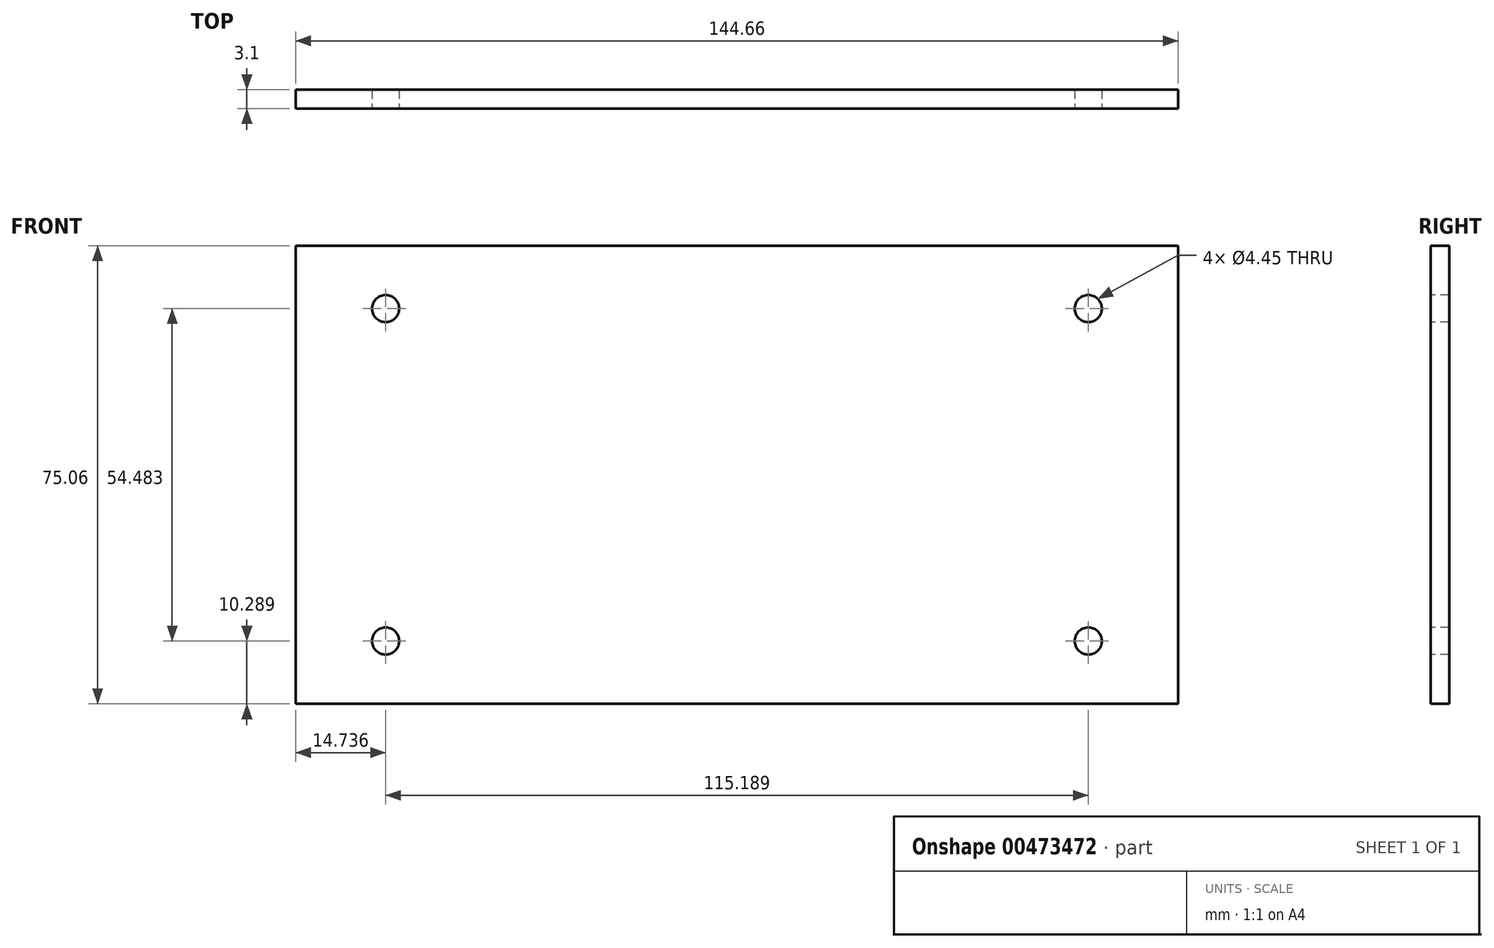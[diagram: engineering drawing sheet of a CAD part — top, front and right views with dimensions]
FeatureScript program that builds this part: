
annotation { "Feature Type Name" : "Feature", "Feature Type Description" : "" }
export const myFeature = defineFeature(function(context is Context, id is Id, definition is map)
    precondition{}
    {
        {
            var Q0;
            Q0=qCreatedBy(makeId("Front.planeOp"),FACE);
            var sketch = newSketch(context, id + "F0", { "sketchPlane" : qUnion([Q0])});
            skLineSegment(sketch, "E0.bottom", {"start": v(-72.33, 37.53) * mm, "end": v(72.33, 37.53) * mm});
            skLineSegment(sketch, "E0.top", {"start": v(-72.33, -37.53) * mm, "end": v(72.33, -37.53) * mm});
            skLineSegment(sketch, "E0.left", {"start": v(-72.33, 37.53) * mm, "end": v(-72.33, -37.53) * mm});
            skLineSegment(sketch, "E0.right", {"start": v(72.33, 37.53) * mm, "end": v(72.33, -37.53) * mm});
            skLineSegment(sketch, "E1", {"start": v(0, 0) * mm, "end": v(0, 37.53) * mm, "construction": true});
            skLineSegment(sketch, "E2", {"start": v(0, 0) * mm, "end": v(0, -37.53) * mm, "construction": true});
            skLineSegment(sketch, "E3", {"start": v(-72.33, 0) * mm, "end": v(0, 0) * mm, "construction": true});
            skLineSegment(sketch, "E4", {"start": v(0, 0) * mm, "end": v(72.33, 0) * mm, "construction": true});
            skSolve(sketch);
        }
        {
            var Q0;
            Q0=makeQuery(id+"F0.imprint","IMPRINT",FACE,{"disambiguationData":[TD([[makeQuery(id+"F0.imprint","IMPRINT",EDGE,{"derivedFrom":sQuery(id+"F0.wireOp",EDGE,"E0.bottom")}),-1.0]])]});
            extrude(context, id + "F1", {"entities" : qUnion([Q0]), "oppositeDirection" : true, "depth" : 3.1 * mm});
        }
        {
            var Q0;
            Q0=makeQuery(id+"F1.opExtrude","CAP_FACE",FACE,{"disambiguationData":[OSD([sQuery(id+"F0.wireOp",EDGE,"E0.bottom"),sQuery(id+"F0.wireOp",EDGE,"E0.top"),sQuery(id+"F0.wireOp",EDGE,"E0.left"),sQuery(id+"F0.wireOp",EDGE,"E0.right")])],"isStart":true});
            var sketch = newSketch(context, id + "F2", { "sketchPlane" : qUnion([Q0])});
            skCircle(sketch, "E5", {"center": v(-57.6, 27.24) * mm, "radius": 2.22 * mm});
            skCircle(sketch, "E6", {"center": v(-57.6, -27.24) * mm, "radius": 2.22 * mm});
            skCircle(sketch, "E7", {"center": v(57.6, -27.24) * mm, "radius": 2.22 * mm});
            skCircle(sketch, "E8", {"center": v(57.6, 27.24) * mm, "radius": 2.22 * mm});
            skSolve(sketch);
        }
        {
            var Q0;
            Q0 = qSketchRegion(id + "F2", true);
            extrude(context, id + "F3", {"entities" : qUnion([Q0]), "operationType" : NewBodyOperationType.REMOVE, "endBound" : BoundingType.UP_TO_NEXT, "oppositeDirection" : true, "depth" : 25.4 * mm});
        }
    });
